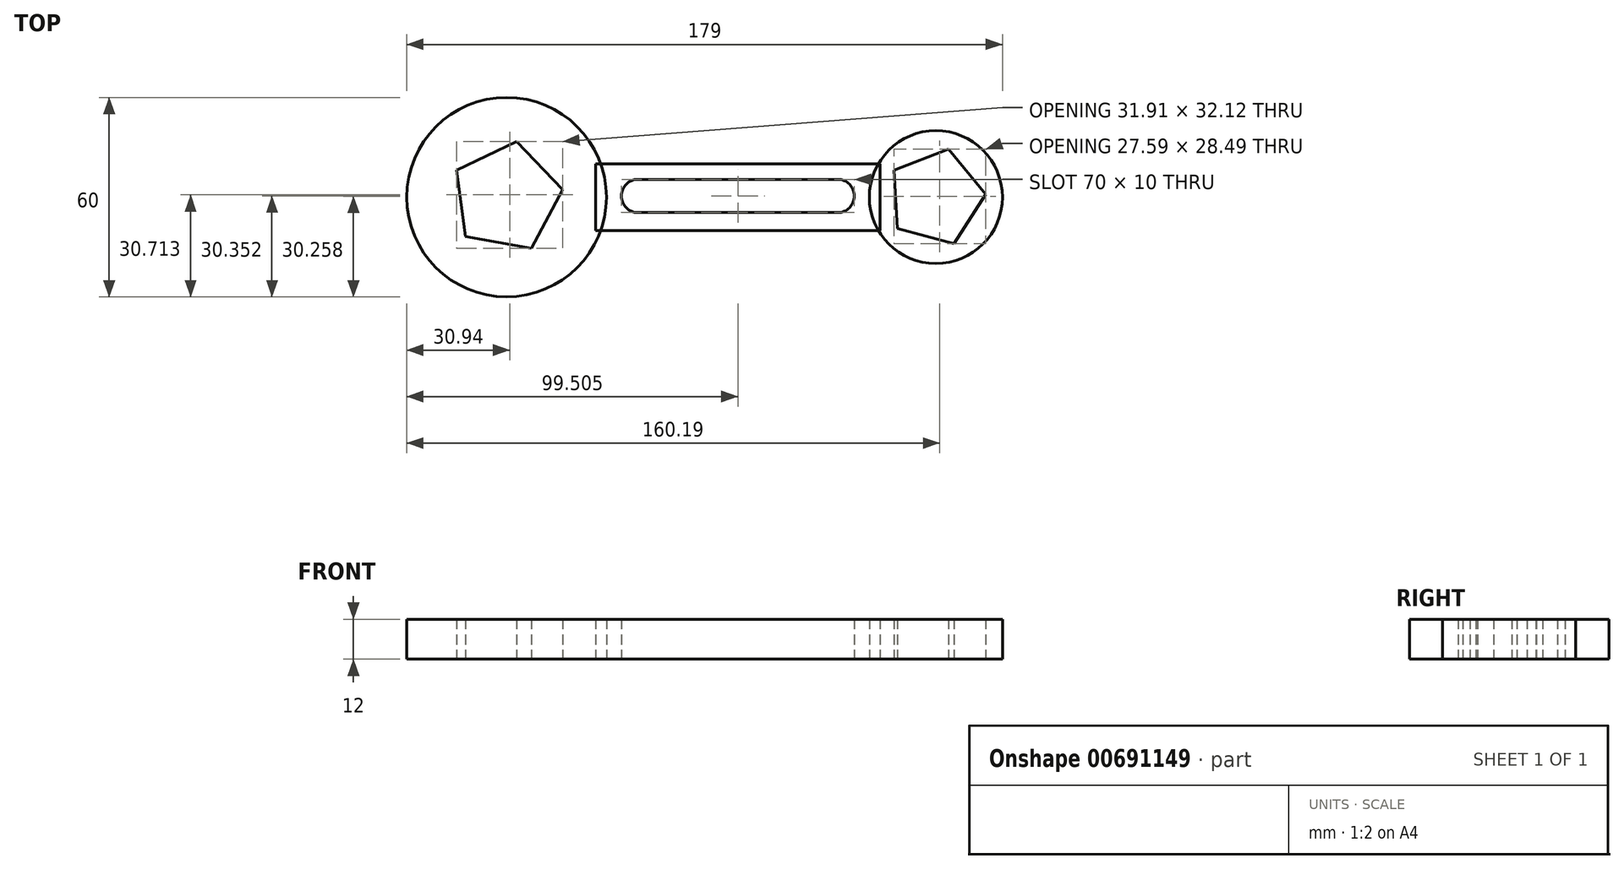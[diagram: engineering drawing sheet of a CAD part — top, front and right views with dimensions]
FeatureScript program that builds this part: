
annotation { "Feature Type Name" : "Feature", "Feature Type Description" : "" }
export const myFeature = defineFeature(function(context is Context, id is Id, definition is map)
    precondition{}
    {
        {
            var Q0;
            Q0=qCreatedBy(makeId("Top.planeOp"),FACE);
            var sketch = newSketch(context, id + "F0", { "sketchPlane" : qUnion([Q0])});
            skCircle(sketch, "E0", {"center": v(-58.68, 0) * mm, "radius": 30 * mm});
            skCircle(sketch, "E1.cCircle", {"center": v(-58.68, 0) * mm, "radius": 13.79 * mm, "construction": true});
            skLineSegment(sketch, "E1.0", {"start": v(-55.65, 16.77) * mm, "end": v(-41.79, 2.3) * mm});
            skLineSegment(sketch, "E1.1", {"start": v(-41.79, 2.3) * mm, "end": v(-51.26, -15.35) * mm});
            skLineSegment(sketch, "E1.2", {"start": v(-51.26, -15.35) * mm, "end": v(-70.98, -11.8) * mm});
            skLineSegment(sketch, "E1.3", {"start": v(-70.98, -11.8) * mm, "end": v(-73.7, 8.06) * mm});
            skLineSegment(sketch, "E1.4", {"start": v(-73.7, 8.06) * mm, "end": v(-55.65, 16.77) * mm});
            skPoint(sketch, "E1.0.midPoint", {"position": v(-48.72, 9.54) * mm});
            skSolve(sketch);
        }
        {
            var Q0;
            Q0=qCreatedBy(makeId("Top.planeOp"),FACE);
            var sketch = newSketch(context, id + "F1", { "sketchPlane" : qUnion([Q0])});
            skCircle(sketch, "E2", {"center": v(70.32, 0) * mm, "radius": 20 * mm});
            skCircle(sketch, "E3.cCircle", {"center": v(70.32, 0) * mm, "radius": 12.14 * mm, "construction": true});
            skLineSegment(sketch, "E3.0", {"start": v(74.16, 14.5) * mm, "end": v(85.3, 0.83) * mm});
            skLineSegment(sketch, "E3.1", {"start": v(85.3, 0.83) * mm, "end": v(75.75, -13.99) * mm});
            skLineSegment(sketch, "E3.2", {"start": v(75.75, -13.99) * mm, "end": v(58.7, -9.48) * mm});
            skLineSegment(sketch, "E3.3", {"start": v(58.7, -9.48) * mm, "end": v(57.72, 8.13) * mm});
            skLineSegment(sketch, "E3.4", {"start": v(57.72, 8.13) * mm, "end": v(74.16, 14.5) * mm});
            skPoint(sketch, "E3.0.midPoint", {"position": v(79.73, 7.67) * mm});
            skSolve(sketch);
        }
        {
            var Q0;
            Q0=qCreatedBy(makeId("Top.planeOp"),FACE);
            var sketch = newSketch(context, id + "F2", { "sketchPlane" : qUnion([Q0])});
            skLineSegment(sketch, "E4.bottom", {"start": v(-31.86, 10) * mm, "end": v(53.6, 10) * mm});
            skLineSegment(sketch, "E4.top", {"start": v(-31.86, -10) * mm, "end": v(53.6, -10) * mm});
            skLineSegment(sketch, "E4.left", {"start": v(-31.86, 10) * mm, "end": v(-31.86, -10) * mm});
            skLineSegment(sketch, "E4.right", {"start": v(53.6, 10) * mm, "end": v(53.6, -10) * mm});
            skLineSegment(sketch, "E5.bottom", {"start": v(-19.18, 5.35) * mm, "end": v(40.82, 5.35) * mm});
            skLineSegment(sketch, "E5.top", {"start": v(-19.18, -4.65) * mm, "end": v(40.82, -4.65) * mm});
            skLineSegment(sketch, "E5.left", {"start": v(-19.18, 5.35) * mm, "end": v(-19.18, -4.65) * mm});
            skLineSegment(sketch, "E5.right", {"start": v(40.82, 5.35) * mm, "end": v(40.82, -4.65) * mm});
            skCircle(sketch, "E6", {"center": v(-19.18, 0.35) * mm, "radius": 5 * mm});
            skCircle(sketch, "E7", {"center": v(40.82, 0.35) * mm, "radius": 5 * mm});
            skSolve(sketch);
        }
        {
            var Q0;
            Q0=makeQuery(id+"F0.imprint","IMPRINT",FACE,{"disambiguationData":[TD([[makeQuery(id+"F0.imprint","IMPRINT",EDGE,{"derivedFrom":sQuery(id+"F0.wireOp",EDGE,"E0")}),1.0]])]});
            var Q1;
            Q1=makeQuery(id+"F2.imprint","IMPRINT",FACE,{"disambiguationData":[TD([[makeQuery(id+"F2.imprint","IMPRINT",EDGE,{"derivedFrom":sQuery(id+"F2.wireOp",EDGE,"E4.bottom")}),-1.0]])]});
            var Q2;
            Q2=makeQuery(id+"F1.imprint","IMPRINT",FACE,{"disambiguationData":[TD([[makeQuery(id+"F1.imprint","IMPRINT",EDGE,{"derivedFrom":sQuery(id+"F1.wireOp",EDGE,"E2")}),1.0]])]});
            extrude(context, id + "F3", {"entities" : qUnion([Q0, Q1, Q2]), "depth" : 12 * mm, "offsetDistance" : 25 * mm});
        }
    });
